# Revit family: STL22954BR_30_40_50
name_source: partatom
category: Luminárias
units: mm (PartAtom-declared; Revit-internal decimal feet)

## family parameters
Compartilhado = Não
Corte com vazios quando carregada = Não
Cota do conector redondo = Utilizar diâmetro
Fonte luminosa = Sim
Hospedeiro = Forro
Manter orientação da anotação = Não
Número OmniClass = 23.80.70.11
Ponto de cálculo do ambiente = Não
Sempre na vertical = Sim
Tipo de parte = Normal
Título OmniClass = Luminaries for Internal Lighting

## types (3) — shared parameters
Altura = 0.05 m
Comprimento = 0.35 m
Dimerização = Não dimerizável
Estrutura = Al - Branco
Fabricante = Stella
Filtro de cor = 16777215
Fluxo Luminoso = 3000 lm
Grau de proteção (IP) = IP20
IRC (Índice de reprodução de cores) = >80
Largura = 0.35 m
Modelo = EDGE
Potência = 26 W
Tensão Elétrica = 100V-240V
Troca de temperatura da cor de lâmpada com esmaecimento = <Nenhum>
URL = https://stella.com.br
Ângulo de Abertura = 110°
Ângulo de inclinação = 90.00°
zero-valued in all types: Elevação padrão

## per-type parameters (varying)
| type | Arquivo de rede fotométrica | Luminoso | Referência | Temperatura da cor (K) |
| STL22954BR/50 - BRANCO - BIVOLT - 5000K - 3000lm - 110° | STELLA - STL22954BR-50 - EDGE 26W.ies | Luminoso - 5000K | STL22954BR/50 - BRANCO - BIVOLT | 5000 K |
| STL22954BR/40 - BRANCO - BIVOLT - 4000K - 3000lm - 110° | STELLA - STL22954BR-40 - EDGE 26W.ies | Luminoso - 4000K | STL22954BR/40 - BRANCO - BIVOLT | 4000 K |
| STL22954BR/30 - BRANCO - BIVOLT - 3000K - 3000lm - 110° | STELLA - STL22954BR-30 - EDGE 26W.ies | Luminoso - 3000K | STL22954BR/30 - BRANCO - BIVOLT | 3000 K |
